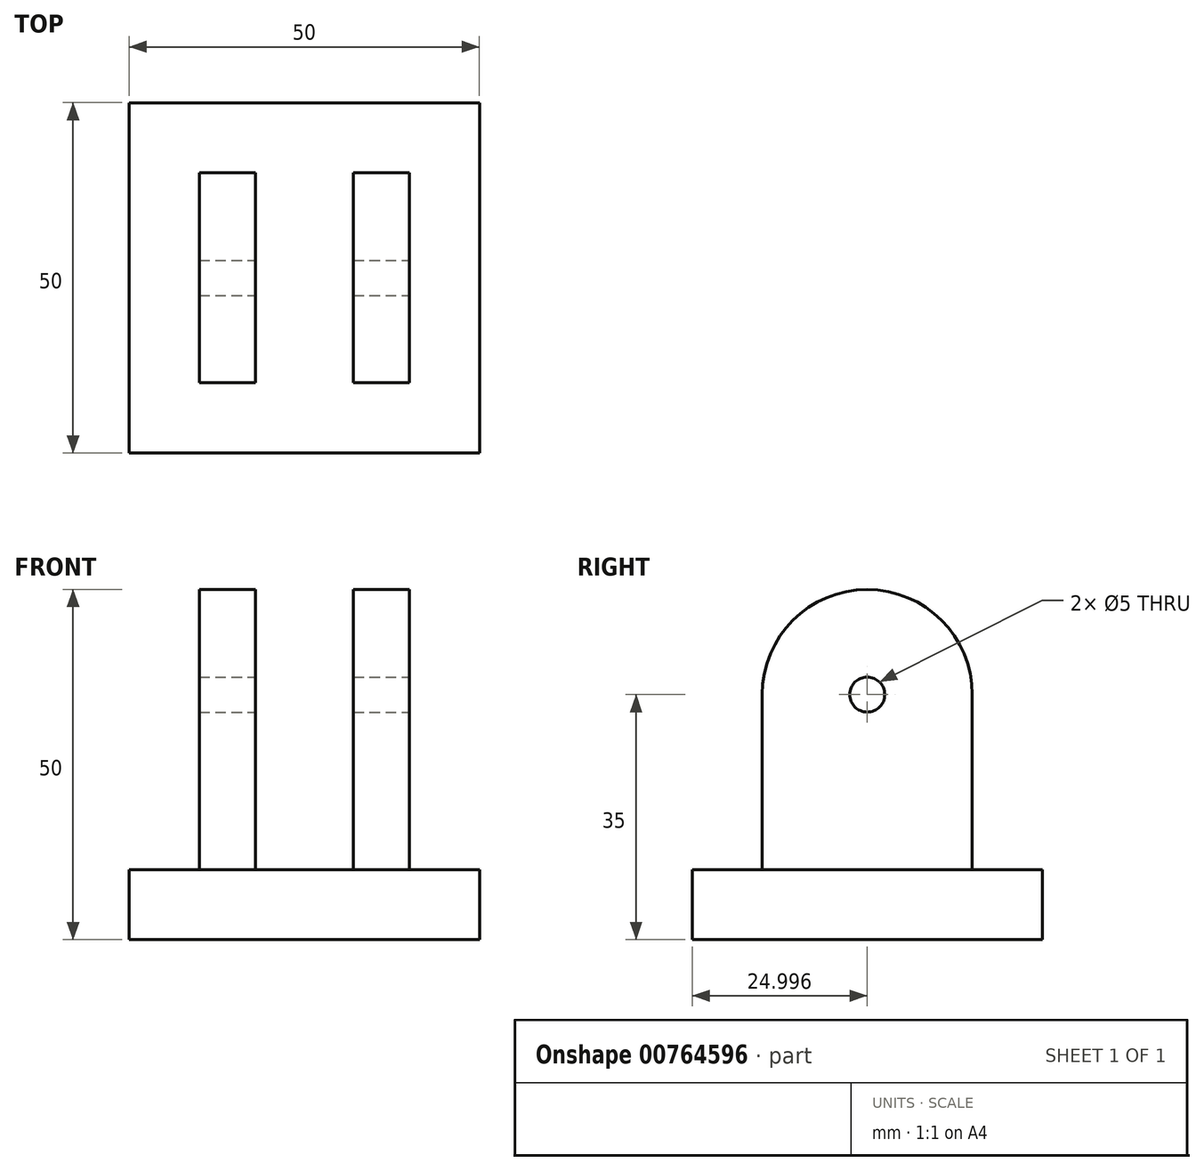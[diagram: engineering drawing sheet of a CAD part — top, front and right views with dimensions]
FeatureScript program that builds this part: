
annotation { "Feature Type Name" : "Feature", "Feature Type Description" : "" }
export const myFeature = defineFeature(function(context is Context, id is Id, definition is map)
    precondition{}
    {
        {
            var Q0;
            Q0=qCreatedBy(makeId("Top.planeOp"),FACE);
            var sketch = newSketch(context, id + "F0", { "sketchPlane" : qUnion([Q0])});
            skLineSegment(sketch, "E0.bottom", {"start": v(-28.59, 22.9) * mm, "end": v(21.41, 22.9) * mm});
            skLineSegment(sketch, "E0.top", {"start": v(-28.59, -27.1) * mm, "end": v(21.41, -27.1) * mm});
            skLineSegment(sketch, "E0.left", {"start": v(-28.59, 22.9) * mm, "end": v(-28.59, -27.1) * mm});
            skLineSegment(sketch, "E0.right", {"start": v(21.41, 22.9) * mm, "end": v(21.41, -27.1) * mm});
            skSolve(sketch);
        }
        {
            var Q0;
            Q0=makeQuery(id+"F0.imprint","IMPRINT",FACE,{"disambiguationData":[TD([[makeQuery(id+"F0.imprint","IMPRINT",EDGE,{"derivedFrom":sQuery(id+"F0.wireOp",EDGE,"E0.bottom")}),-1.0]])]});
            extrude(context, id + "F1", {"entities" : qUnion([Q0]), "depth" : 10 * mm, "offsetDistance" : 25 * mm});
        }
        {
            var Q0;
            Q0=qCreatedBy(makeId("Top.planeOp"),FACE);
            var sketch = newSketch(context, id + "F2", { "sketchPlane" : qUnion([Q0])});
            skLineSegment(sketch, "E1.bottom", {"start": v(-18.59, 12.9) * mm, "end": v(-10.59, 12.9) * mm});
            skLineSegment(sketch, "E1.top", {"start": v(-18.59, -17.1) * mm, "end": v(-10.59, -17.1) * mm});
            skLineSegment(sketch, "E1.left", {"start": v(-18.59, 12.9) * mm, "end": v(-18.59, -17.1) * mm});
            skLineSegment(sketch, "E1.right", {"start": v(-10.59, 12.9) * mm, "end": v(-10.59, -17.1) * mm});
            skLineSegment(sketch, "E2.bottom", {"start": v(3.41, 12.9) * mm, "end": v(11.41, 12.9) * mm});
            skLineSegment(sketch, "E2.top", {"start": v(3.41, -17.1) * mm, "end": v(11.41, -17.1) * mm});
            skLineSegment(sketch, "E2.left", {"start": v(3.41, 12.9) * mm, "end": v(3.41, -17.1) * mm});
            skLineSegment(sketch, "E2.right", {"start": v(11.41, 12.9) * mm, "end": v(11.41, -17.1) * mm});
            skSolve(sketch);
        }
        {
            var Q0;
            Q0 = qSketchRegion(id + "F2", true);
            extrude(context, id + "F3", {"entities" : qUnion([Q0]), "operationType" : NewBodyOperationType.ADD, "depth" : 50 * mm, "offsetDistance" : 25 * mm});
        }
        {
            var Q0;
            Q0=makeQuery(id+"F3.opExtrude","CAP_EDGE",EDGE,{"disambiguationData":[OSD([sQuery(id+"F2.wireOp",EDGE,"E1.top")])],"isStart":false});
            var Q1;
            Q1=makeQuery(id+"F3.opExtrude","CAP_EDGE",EDGE,{"disambiguationData":[OSD([sQuery(id+"F2.wireOp",EDGE,"E1.bottom")])],"isStart":false});
            var Q2;
            Q2=makeQuery(id+"F3.opExtrude","CAP_EDGE",EDGE,{"disambiguationData":[OSD([sQuery(id+"F2.wireOp",EDGE,"E2.top")])],"isStart":false});
            var Q3;
            Q3=makeQuery(id+"F3.opExtrude","CAP_EDGE",EDGE,{"disambiguationData":[OSD([sQuery(id+"F2.wireOp",EDGE,"E2.bottom")])],"isStart":false});
            fillet(context, id + "F4", {"entities" : qUnion([Q0, Q1, Q2, Q3]), "radius" : 15 * mm, "tangentPropagation" : true, "allowEdgeOverflow" : false});
        }
        {
            var Q0;
            Q0=makeQuery(id+"F3.opExtrude","SWEPT_FACE",FACE,{"disambiguationData":[OSD([sQuery(id+"F2.wireOp",EDGE,"E2.right")])]});
            var sketch = newSketch(context, id + "F5", { "sketchPlane" : qUnion([Q0])});
            skPoint(sketch, "E3", {"position": v(-2.1, 35) * mm});
            skSolve(sketch);
        }
        {
            var Q0;
            Q0=sQuery(id+"F5.wireOp",VERTEX,"E3");
            var Q1;
            Q1=makeQuery(id+"F1.opExtrude","SWEPT_BODY",BODY,{"disambiguationData":[OSD([sQuery(id+"F0.wireOp",EDGE,"E0.bottom"),sQuery(id+"F0.wireOp",EDGE,"E0.top"),sQuery(id+"F0.wireOp",EDGE,"E0.left"),sQuery(id+"F0.wireOp",EDGE,"E0.right")])]});
            hole(context, id + "F6", {"style" : HoleStyle.SIMPLE, "endStyle" : HoleEndStyle.THROUGH, "holeDiameter" : 5 * mm, "majorDiameter" : 5 * mm, "isTappedThrough" : true, "tappedDepth" : 12 * mm, "tapClearance" : 3, "locations" : qUnion([Q0]), "scope" : qUnion([Q1])});
        }
    });
